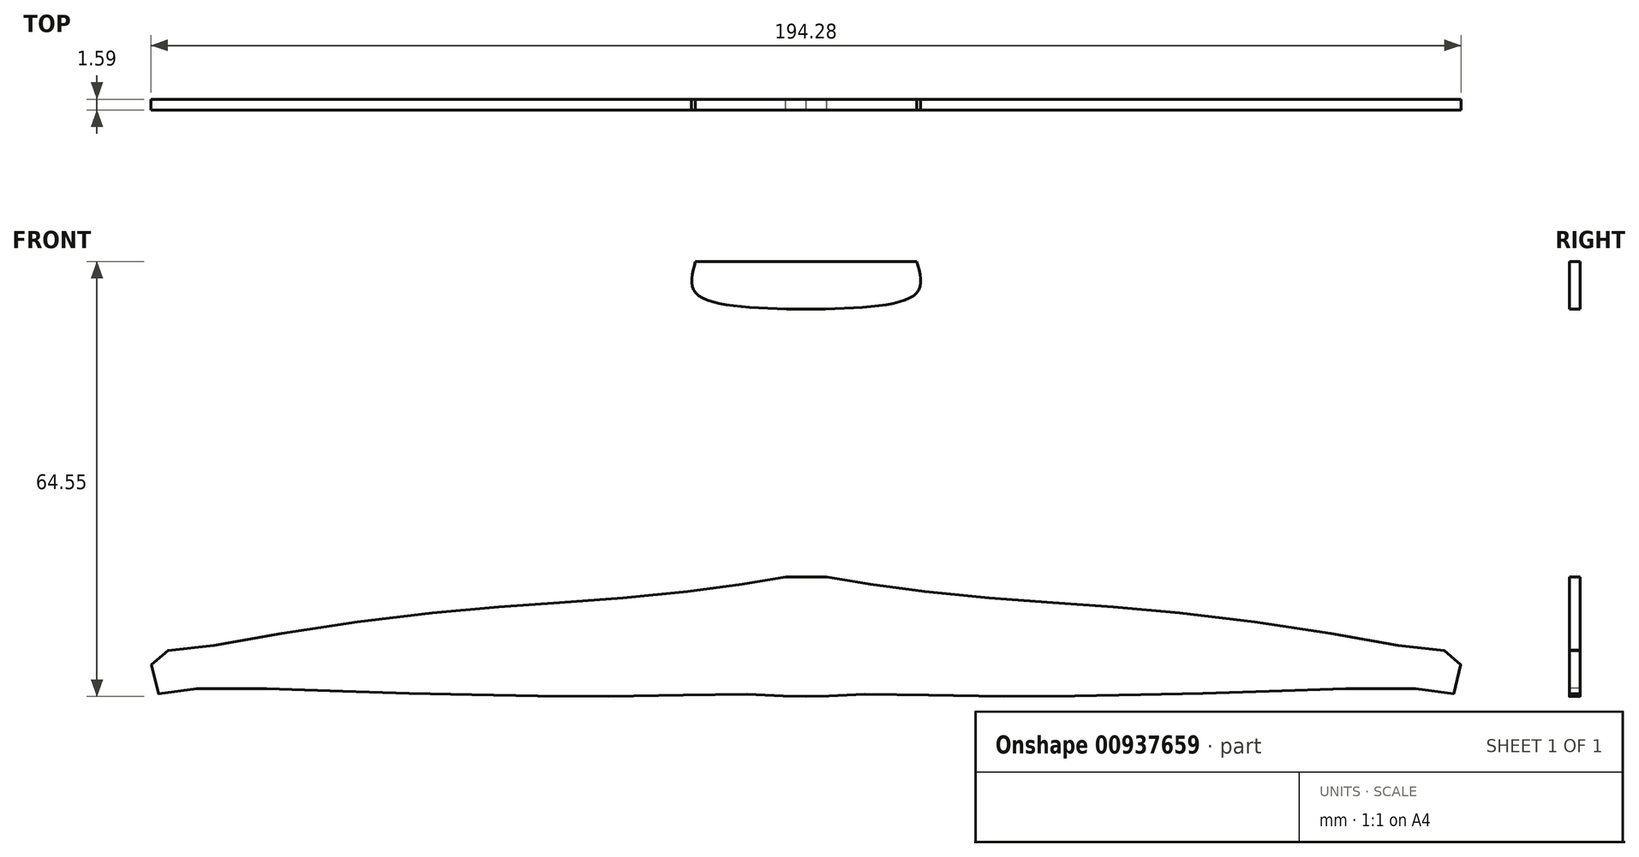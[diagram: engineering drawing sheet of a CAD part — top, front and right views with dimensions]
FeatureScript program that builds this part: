
annotation { "Feature Type Name" : "Feature", "Feature Type Description" : "" }
export const myFeature = defineFeature(function(context is Context, id is Id, definition is map)
    precondition{}
    {
        {
            var Q0;
            Q0=qCreatedBy(makeId("Front.planeOp"),FACE);
            var sketch = newSketch(context, id + "F0", { "sketchPlane" : qUnion([Q0])});
            skLineSegment(sketch, "E0.bottom", {"start": v(114.3, -50.8) * mm, "end": v(-114.3, -50.8) * mm, "construction": true});
            skLineSegment(sketch, "E0.top", {"start": v(114.3, 50.8) * mm, "end": v(-114.3, 50.8) * mm, "construction": true});
            skLineSegment(sketch, "E0.left", {"start": v(114.3, -50.8) * mm, "end": v(114.3, 50.8) * mm, "construction": true});
            skLineSegment(sketch, "E0.right", {"start": v(-114.3, -50.8) * mm, "end": v(-114.3, 50.8) * mm, "construction": true});
            skPoint(sketch, "E0.middle", {"position": v(0, 0) * mm});
            skPoint(sketch, "E1.middle", {"position": v(0, -10.6) * mm});
            skLineSegment(sketch, "E2", {"start": v(-96.63, -17.13) * mm, "end": v(114.3, -17.13) * mm, "construction": true});
            skFitSpline(sketch, "E3", {"points": [v(-3.06, -3.52) * mm, v(-13.4, -5.15) * mm, v(-32.73, -7.06) * mm, v(-51.24, -8.42) * mm, v(-78.2, -11.96) * mm, v(-94.26, -14.4) * mm, v(-96.63, -14.95) * mm, v(-96.63, -20.4) * mm, v(-93.44, -20.4) * mm, v(-70.57, -20.4) * mm, v(-50.16, -20.94) * mm, v(-27.29, -21.21) * mm, v(-6.6, -20.94) * mm, v(-2.52, -21.21) * mm, v(0, -21.21) * mm], "startDerivative": vector(-142.59, -25.04) * mm, "endDerivative": vector(77.65, 1.95) * mm});
            skLineSegment(sketch, "E4", {"start": v(0, -50.8) * mm, "end": v(0, 50.8) * mm, "construction": true});
            skFitSpline(sketch, "E5.MirrorCS", {"points": [v(3.06, -3.52) * mm, v(13.4, -5.15) * mm, v(32.73, -7.06) * mm, v(51.24, -8.42) * mm, v(78.2, -11.96) * mm, v(94.26, -14.4) * mm, v(96.63, -14.95) * mm, v(96.63, -20.4) * mm, v(93.44, -20.4) * mm, v(70.57, -20.4) * mm, v(50.16, -20.94) * mm, v(27.29, -21.21) * mm, v(6.6, -20.94) * mm, v(2.52, -21.21) * mm, v(0, -21.21) * mm], "startDerivative": vector(142.59, -25.04) * mm, "endDerivative": vector(-77.65, 1.95) * mm});
            skFitSpline(sketch, "E6", {"points": [v(3.06, -3.52) * mm, v(-3.06, -3.52) * mm], "startDerivative": vector(-6.12, 0) * mm, "endDerivative": vector(-6.12, 0) * mm});
            skFitSpline(sketch, "E7", {"points": [v(-16.4, 43.3) * mm, v(-16.4, 38.68) * mm, v(0, 36.23) * mm], "startDerivative": vector(-4.33, -15.05) * mm, "endDerivative": vector(33.26, -0.59) * mm});
            skFitSpline(sketch, "E8", {"points": [v(-16.4, 43.3) * mm, v(0, 43.3) * mm], "startDerivative": vector(16.4, 0) * mm, "endDerivative": vector(16.4, 0) * mm});
            skFitSpline(sketch, "E9.MirrorCS", {"points": [v(16.4, 43.3) * mm, v(0, 43.3) * mm], "startDerivative": vector(-16.4, 0) * mm, "endDerivative": vector(-16.4, 0) * mm});
            skFitSpline(sketch, "E10.MirrorCS", {"points": [v(16.4, 43.3) * mm, v(16.4, 38.68) * mm, v(0, 36.23) * mm], "startDerivative": vector(4.33, -15.05) * mm, "endDerivative": vector(-33.26, -0.59) * mm});
            skSolve(sketch);
        }
        {
            var Q0;
            Q0 = qSketchRegion(id + "F0", true);
            extrude(context, id + "F1", {"entities" : qUnion([Q0]), "depth" : 1.59 * mm, "offsetDistance" : 25.4 * mm});
        }
    });
